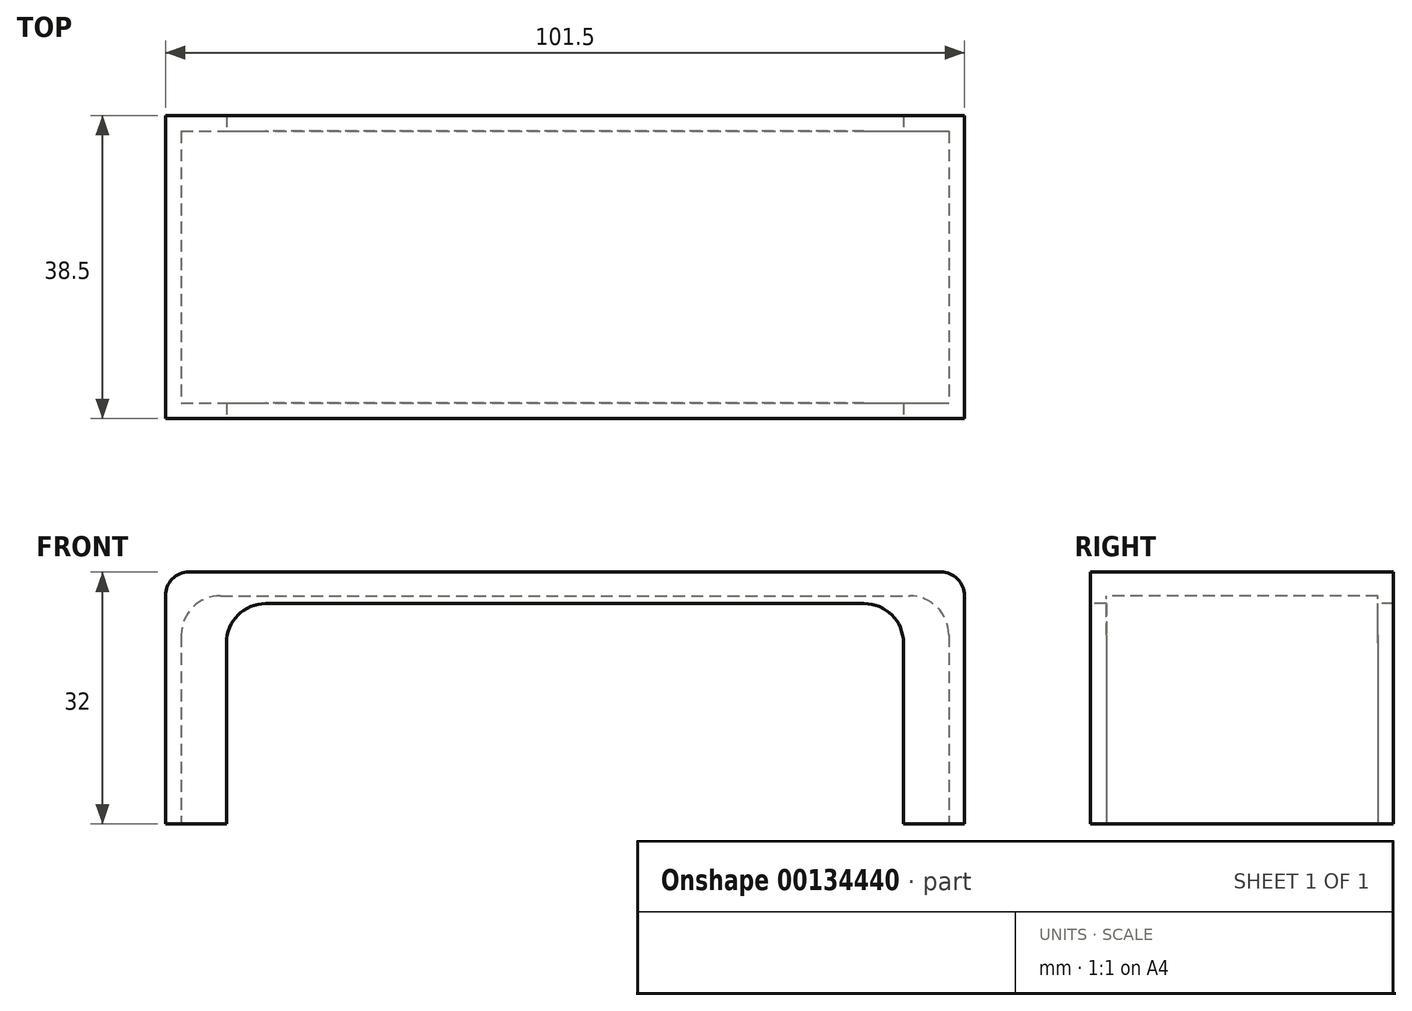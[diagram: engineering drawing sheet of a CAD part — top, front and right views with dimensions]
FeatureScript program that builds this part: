
annotation { "Feature Type Name" : "Feature", "Feature Type Description" : "" }
export const myFeature = defineFeature(function(context is Context, id is Id, definition is map)
    precondition{}
    {
        {
            var Q0;
            Q0=qCreatedBy(makeId("Top.planeOp"),FACE);
            var sketch = newSketch(context, id + "F0", { "sketchPlane" : qUnion([Q0])});
            skLineSegment(sketch, "E0.bottom", {"start": v(-50.75, 19.25) * mm, "end": v(50.75, 19.25) * mm});
            skLineSegment(sketch, "E0.top", {"start": v(-50.75, -19.25) * mm, "end": v(50.75, -19.25) * mm});
            skLineSegment(sketch, "E0.left", {"start": v(-50.75, 19.25) * mm, "end": v(-50.75, -19.25) * mm});
            skLineSegment(sketch, "E0.right", {"start": v(50.75, 19.25) * mm, "end": v(50.75, -19.25) * mm});
            skSolve(sketch);
        }
        {
            var Q0;
            Q0 = qSketchRegion(id + "F0", true);
            extrude(context, id + "F1", {"entities" : qUnion([Q0]), "depth" : 32 * mm});
        }
        {
            var Q0;
            Q0=makeQuery(id+"F1.opExtrude","CAP_FACE",FACE,{"disambiguationData":[OSD([sQuery(id+"F0.wireOp",EDGE,"E0.bottom"),sQuery(id+"F0.wireOp",EDGE,"E0.top"),sQuery(id+"F0.wireOp",EDGE,"E0.left"),sQuery(id+"F0.wireOp",EDGE,"E0.right")])],"isStart":true});
            var sketch = newSketch(context, id + "F2", { "sketchPlane" : qUnion([Q0])});
            skLineSegment(sketch, "E1.0", {"start": v(-48.75, 17.25) * mm, "end": v(48.75, 17.25) * mm});
            skLineSegment(sketch, "E1.1", {"start": v(-48.75, -17.25) * mm, "end": v(-48.75, 17.25) * mm});
            skLineSegment(sketch, "E1.2", {"start": v(-48.75, -17.25) * mm, "end": v(48.75, -17.25) * mm});
            skLineSegment(sketch, "E1.3", {"start": v(48.75, -17.25) * mm, "end": v(48.75, 17.25) * mm});
            skSolve(sketch);
        }
        {
            var Q0;
            Q0 = qSketchRegion(id + "F2", true);
            extrude(context, id + "F3", {"entities" : qUnion([Q0]), "operationType" : NewBodyOperationType.REMOVE, "oppositeDirection" : true, "depth" : 29 * mm});
        }
        {
            var Q0;
            Q0=makeQuery(id+"F1.opExtrude","SWEPT_FACE",FACE,{"disambiguationData":[OSD([sQuery(id+"F0.wireOp",EDGE,"E0.top")])]});
            var sketch = newSketch(context, id + "F4", { "sketchPlane" : qUnion([Q0])});
            skLineSegment(sketch, "E2.bottom", {"start": v(-43, 0) * mm, "end": v(43, 0) * mm});
            skLineSegment(sketch, "E2.top", {"start": v(-38, 28) * mm, "end": v(38, 28) * mm});
            skLineSegment(sketch, "E2.left", {"start": v(-43, 0) * mm, "end": v(-43, 23) * mm});
            skLineSegment(sketch, "E2.right", {"start": v(43, 0) * mm, "end": v(43, 23) * mm});
            skPoint(sketch, "E3.visualSharp", {"position": v(-43, 28) * mm});
            skArc(sketch, "E3.filletArc", {"start": v(-38, 28) * mm, "mid": v(-41.54, 26.54) * mm, "end": v(-43, 23) * mm});
            skPoint(sketch, "E4.visualSharp", {"position": v(43, 28) * mm});
            skArc(sketch, "E4.filletArc", {"start": v(43, 23) * mm, "mid": v(41.54, 26.54) * mm, "end": v(38, 28) * mm});
            skSolve(sketch);
        }
        {
            var Q0;
            Q0 = qSketchRegion(id + "F4", true);
            extrude(context, id + "F5", {"entities" : qUnion([Q0]), "operationType" : NewBodyOperationType.REMOVE, "endBound" : BoundingType.THROUGH_ALL, "oppositeDirection" : true, "depth" : 25 * mm});
        }
        {
            var Q0;
            Q0=makeQuery(id+"F3.boolean.opBoolean","COPY",EDGE,{"derivedFrom":makeQuery(id+"F3.opExtrude","CAP_EDGE",EDGE,{"disambiguationData":[OSD([sQuery(id+"F2.wireOp",EDGE,"E1.3")])],"isStart":false})});
            fillet(context, id + "F6", {"entities" : qUnion([Q0]), "radius" : 5 * mm, "tangentPropagation" : true, "allowEdgeOverflow" : false});
        }
        {
            var Q0;
            Q0=makeQuery(id+"F3.boolean.opBoolean","COPY",EDGE,{"derivedFrom":makeQuery(id+"F3.opExtrude","CAP_EDGE",EDGE,{"disambiguationData":[OSD([sQuery(id+"F2.wireOp",EDGE,"E1.1")])],"isStart":false})});
            fillet(context, id + "F7", {"entities" : qUnion([Q0]), "radius" : 5 * mm, "tangentPropagation" : true, "allowEdgeOverflow" : false});
        }
        {
            var Q0;
            Q0=makeQuery(id+"F1.opExtrude","CAP_EDGE",EDGE,{"disambiguationData":[OSD([sQuery(id+"F0.wireOp",EDGE,"E0.right")])],"isStart":false});
            var Q1;
            Q1=makeQuery(id+"F1.opExtrude","CAP_EDGE",EDGE,{"disambiguationData":[OSD([sQuery(id+"F0.wireOp",EDGE,"E0.left")])],"isStart":false});
            fillet(context, id + "F8", {"entities" : qUnion([Q0, Q1]), "radius" : 3 * mm, "tangentPropagation" : true, "allowEdgeOverflow" : false});
        }
    });
